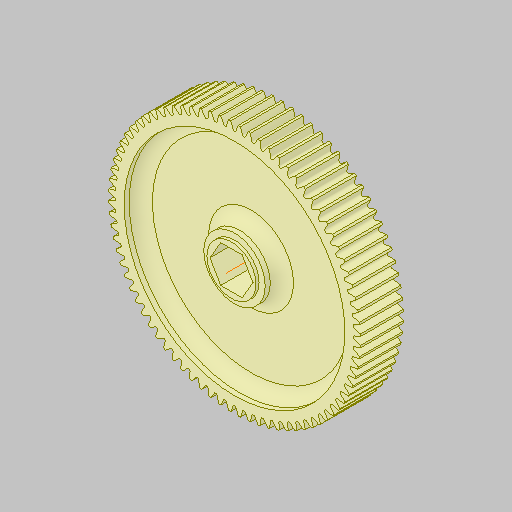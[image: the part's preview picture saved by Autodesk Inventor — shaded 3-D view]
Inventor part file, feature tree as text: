
AUTODESK INVENTOR PART (.ipt)
format: ipt  version: 2023.5 (Build 275446000, 446)  size: 719,360 bytes
history: native  units: in
note: dims shown in document units (in); Inventor stores cm internally (conversion verified against a paired STEP export)
features: mirror x1
ambient origin geometry x8: Origin, YZ Plane, XZ Plane, XY Plane, X Axis, Y Axis, Z Axis, Center Point
bodies: Solid1 (feature_tree)
feature tree (1):
  mirror  "Mirror1"
